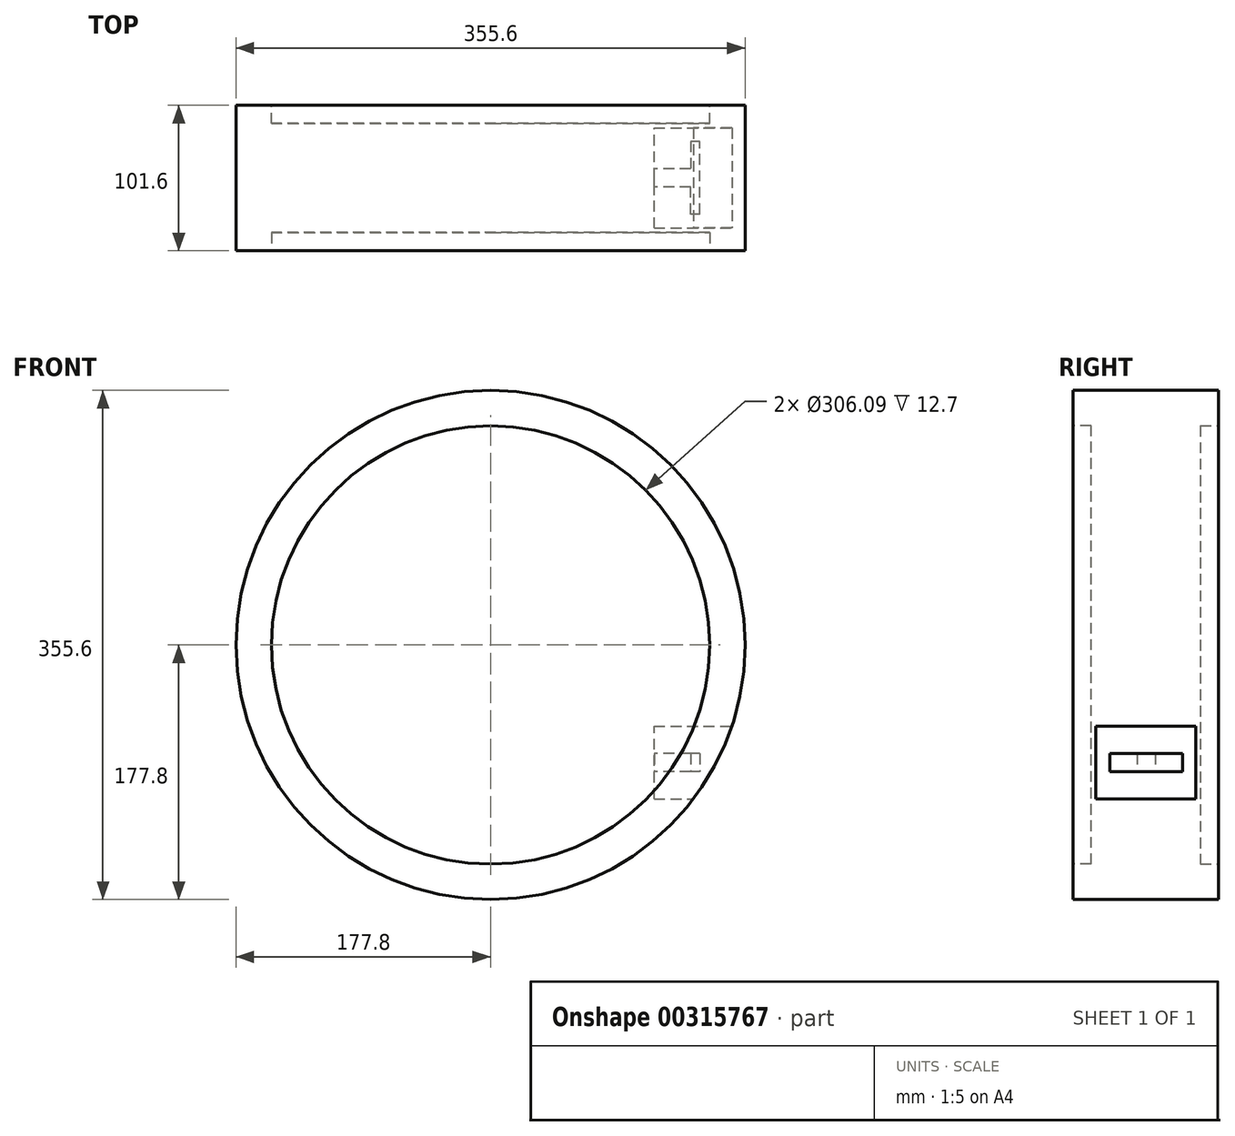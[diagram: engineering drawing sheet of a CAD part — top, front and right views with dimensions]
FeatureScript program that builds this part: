
annotation { "Feature Type Name" : "Feature", "Feature Type Description" : "" }
export const myFeature = defineFeature(function(context is Context, id is Id, definition is map)
    precondition{}
    {
        {
            var Q0;
            Q0=qCreatedBy(makeId("Front.planeOp"),FACE);
            var sketch = newSketch(context, id + "F0", { "sketchPlane" : qUnion([Q0])});
            skCircle(sketch, "E0", {"center": v(0, 0) * mm, "radius": 177.8 * mm});
            skSolve(sketch);
        }
        {
            var Q0;
            Q0=makeQuery(id+"F0.imprint","IMPRINT",FACE,{"disambiguationData":[TD([[makeQuery(id+"F0.imprint","IMPRINT",EDGE,{"derivedFrom":sQuery(id+"F0.wireOp",EDGE,"E0")}),1.0]])]});
            extrude(context, id + "F1", {"entities" : qUnion([Q0]), "oppositeDirection" : true, "depth" : 101.6 * mm});
        }
        {
            var Q0;
            Q0=makeQuery(id+"F1.opExtrude","CAP_FACE",FACE,{"disambiguationData":[OSD([sQuery(id+"F0.wireOp",EDGE,"E0")])],"isStart":true});
            var sketch = newSketch(context, id + "F2", { "sketchPlane" : qUnion([Q0])});
            skCircle(sketch, "E1", {"center": v(0, 0) * mm, "radius": 153.04 * mm});
            skSolve(sketch);
        }
        {
            var Q0;
            Q0=makeQuery(id+"F2.imprint","IMPRINT",FACE,{"disambiguationData":[TD([[makeQuery(id+"F2.imprint","IMPRINT",EDGE,{"derivedFrom":sQuery(id+"F2.wireOp",EDGE,"E1")}),1.0]])]});
            extrude(context, id + "F3", {"entities" : qUnion([Q0]), "operationType" : NewBodyOperationType.REMOVE, "oppositeDirection" : true, "depth" : 12.7 * mm});
        }
        {
            var Q0;
            Q0=makeQuery(id+"F1.opExtrude","CAP_FACE",FACE,{"disambiguationData":[OSD([sQuery(id+"F0.wireOp",EDGE,"E0")])],"isStart":false});
            var sketch = newSketch(context, id + "F4", { "sketchPlane" : qUnion([Q0])});
            skCircle(sketch, "E2", {"center": v(0, 0) * mm, "radius": 153.04 * mm});
            skSolve(sketch);
        }
        {
            var Q0;
            Q0=makeQuery(id+"F4.imprint","IMPRINT",FACE,{"disambiguationData":[TD([[makeQuery(id+"F4.imprint","IMPRINT",EDGE,{"derivedFrom":sQuery(id+"F4.wireOp",EDGE,"E2")}),1.0]])]});
            extrude(context, id + "F5", {"entities" : qUnion([Q0]), "operationType" : NewBodyOperationType.REMOVE, "oppositeDirection" : true, "depth" : 12.7 * mm});
        }
        {
            var Q0;
            Q0=qCreatedBy(makeId("Right.planeOp"),FACE);
            cPlane(context, id + "F6", {"entities" : qUnion([Q0]), "cplaneType" : CPlaneType.OFFSET, "offset" : 177.8 * mm, "width" : 152.4 * mm, "height" : 152.4 * mm});
        }
        {
            var Q0;
            Q0=qCreatedBy(id+"F6.planeOp",FACE);
            var sketch = newSketch(context, id + "F7", { "sketchPlane" : qUnion([Q0])});
            skLineSegment(sketch, "E3.bottom", {"start": v(15.93, -107.48) * mm, "end": v(85.78, -107.48) * mm});
            skLineSegment(sketch, "E3.top", {"start": v(15.93, -56.68) * mm, "end": v(85.78, -56.68) * mm});
            skLineSegment(sketch, "E3.left", {"start": v(15.93, -107.48) * mm, "end": v(15.93, -56.68) * mm});
            skLineSegment(sketch, "E3.right", {"start": v(85.78, -107.48) * mm, "end": v(85.78, -56.68) * mm});
            skPoint(sketch, "E3.middle", {"position": v(50.86, -82.08) * mm});
            skSolve(sketch);
        }
        {
            var Q0;
            Q0=makeQuery(id+"F7.imprint","IMPRINT",FACE,{"disambiguationData":[TD([[makeQuery(id+"F7.imprint","IMPRINT",EDGE,{"derivedFrom":sQuery(id+"F7.wireOp",EDGE,"E3.bottom")}),1.0]])]});
            extrude(context, id + "F8", {"entities" : qUnion([Q0]), "operationType" : NewBodyOperationType.REMOVE, "oppositeDirection" : true, "depth" : 63.5 * mm});
        }
        {
            var Q0;
            Q0=qCreatedBy(makeId("Right.planeOp"),FACE);
            cPlane(context, id + "F9", {"entities" : qUnion([Q0]), "cplaneType" : CPlaneType.OFFSET, "offset" : 114.3 * mm, "width" : 152.4 * mm, "height" : 152.4 * mm});
        }
        {
            var Q0;
            Q0=qCreatedBy(id+"F9.planeOp",FACE);
            var sketch = newSketch(context, id + "F10", { "sketchPlane" : qUnion([Q0])});
            skLineSegment(sketch, "E4.bottom", {"start": v(44.68, -75.9) * mm, "end": v(57.38, -75.9) * mm});
            skLineSegment(sketch, "E4.top", {"start": v(44.68, -88.6) * mm, "end": v(57.38, -88.6) * mm});
            skLineSegment(sketch, "E4.left", {"start": v(44.68, -75.9) * mm, "end": v(44.68, -88.6) * mm});
            skLineSegment(sketch, "E4.right", {"start": v(57.38, -75.9) * mm, "end": v(57.38, -88.6) * mm});
            skPoint(sketch, "E4.middle", {"position": v(51.03, -82.26) * mm});
            skSolve(sketch);
        }
        {
            var Q0;
            Q0=makeQuery(id+"F10.imprint","IMPRINT",FACE,{"disambiguationData":[TD([[makeQuery(id+"F10.imprint","IMPRINT",EDGE,{"derivedFrom":sQuery(id+"F10.wireOp",EDGE,"E4.bottom")}),-1.0]])]});
            extrude(context, id + "F11", {"entities" : qUnion([Q0]), "operationType" : NewBodyOperationType.ADD, "depth" : 31.75 * mm});
        }
        {
            var Q0;
            Q0=makeQuery(id+"F11.opExtrude","SWEPT_FACE",FACE,{"disambiguationData":[OSD([sQuery(id+"F10.wireOp",EDGE,"E4.left")])]});
            var sketch = newSketch(context, id + "F12", { "sketchPlane" : qUnion([Q0])});
            skLineSegment(sketch, "E5.bottom", {"start": v(146.05, -75.9) * mm, "end": v(139.7, -75.9) * mm});
            skLineSegment(sketch, "E5.top", {"start": v(146.05, -88.6) * mm, "end": v(139.7, -88.6) * mm});
            skLineSegment(sketch, "E5.left", {"start": v(146.05, -75.9) * mm, "end": v(146.05, -88.6) * mm});
            skLineSegment(sketch, "E5.right", {"start": v(139.7, -75.9) * mm, "end": v(139.7, -88.6) * mm});
            skSolve(sketch);
        }
        {
            var Q0;
            Q0=makeQuery(id+"F12.imprint","IMPRINT",FACE,{"disambiguationData":[TD([[makeQuery(id+"F12.imprint","IMPRINT",EDGE,{"derivedFrom":sQuery(id+"F12.wireOp",EDGE,"E5.bottom")}),1.0]])]});
            extrude(context, id + "F13", {"entities" : qUnion([Q0]), "operationType" : NewBodyOperationType.ADD, "depth" : 19.05 * mm});
        }
        {
            var Q0;
            Q0=makeQuery(id+"F11.opExtrude","SWEPT_FACE",FACE,{"disambiguationData":[OSD([sQuery(id+"F10.wireOp",EDGE,"E4.right")])]});
            var sketch = newSketch(context, id + "F14", { "sketchPlane" : qUnion([Q0])});
            skLineSegment(sketch, "E6.bottom", {"start": v(-146.05, -75.9) * mm, "end": v(-139.7, -75.9) * mm});
            skLineSegment(sketch, "E6.top", {"start": v(-146.05, -88.6) * mm, "end": v(-139.7, -88.6) * mm});
            skLineSegment(sketch, "E6.left", {"start": v(-146.05, -75.9) * mm, "end": v(-146.05, -88.6) * mm});
            skLineSegment(sketch, "E6.right", {"start": v(-139.7, -75.9) * mm, "end": v(-139.7, -88.6) * mm});
            skSolve(sketch);
        }
        {
            var Q0;
            Q0=makeQuery(id+"F14.imprint","IMPRINT",FACE,{"disambiguationData":[TD([[makeQuery(id+"F14.imprint","IMPRINT",EDGE,{"derivedFrom":sQuery(id+"F14.wireOp",EDGE,"E6.bottom")}),-1.0]])]});
            extrude(context, id + "F15", {"entities" : qUnion([Q0]), "operationType" : NewBodyOperationType.ADD, "depth" : 19.05 * mm});
        }
    });
